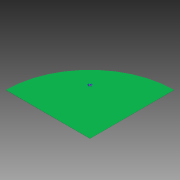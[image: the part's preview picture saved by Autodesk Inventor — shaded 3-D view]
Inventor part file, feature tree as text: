
AUTODESK INVENTOR PART (.ipt)
format: ipt  version: 2011 SP1 (Build 150282100, 282)  size: 100,352 bytes
history: native  units: mm
features: extrude x2, fillet x1, sketch x1, other x1
ambient origin geometry x8: Origin, YZ Plane, XZ Plane, XY Plane, X Axis, Y Axis, Z Axis, Center Point
bodies: Solid1 (feature_tree)
feature tree (5):
  extrude  "Wafer"  Depth=0.1mm TaperAngle=0.0deg
  fillet  "OuterEdge"  Radius=0.1mm
  extrude  "ThroughWaferEtch"  Depth=20.0mm
  sketch  "Sketch1"  dims[d0=50.0mm d1=0.1mm d2=0.0mm d3=0.1mm d4=20.0mm d5=20.0mm d6=10.0mm d7=0.75mm d10=0.1mm d11=-10.053096mm d12=2.5mm d13=2.5mm]
  other  "DeepEtchSketch"
